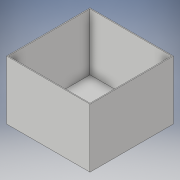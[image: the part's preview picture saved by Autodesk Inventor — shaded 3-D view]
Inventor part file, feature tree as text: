
AUTODESK INVENTOR PART (.ipt)
format: ipt  version: 2018 (Build 220112000, 112)  size: 110,080 bytes
history: native  units: in
note: dims shown in document units (in); Inventor stores cm internally (conversion verified against a paired STEP export)
features: extrude x3, sketch x3
ambient origin geometry x8: Origin, YZ Plane, XZ Plane, XY Plane, X Axis, Y Axis, Z Axis, Center Point
bodies: Solid1 (feature_tree)
feature tree (6):
  extrude  "Extrusion1"  Depth=4.76in
  extrude  "Extrusion2"  Depth=4.66in
  extrude  "Extrusion3"  Depth=3.26in TaperAngle=0.0deg
  sketch  "Sketch1"  dims[d0=4.76in d1=4.76in]
  sketch  "Sketch2"  dims[d2=0.1in d3=0.0in d4=4.66in]
  sketch  "Sketch3"  dims[d5=4.66in d6=3.26in d7=0.0in d10=0.164in d11=0.164in d12=0.0in d13=0.0in]
